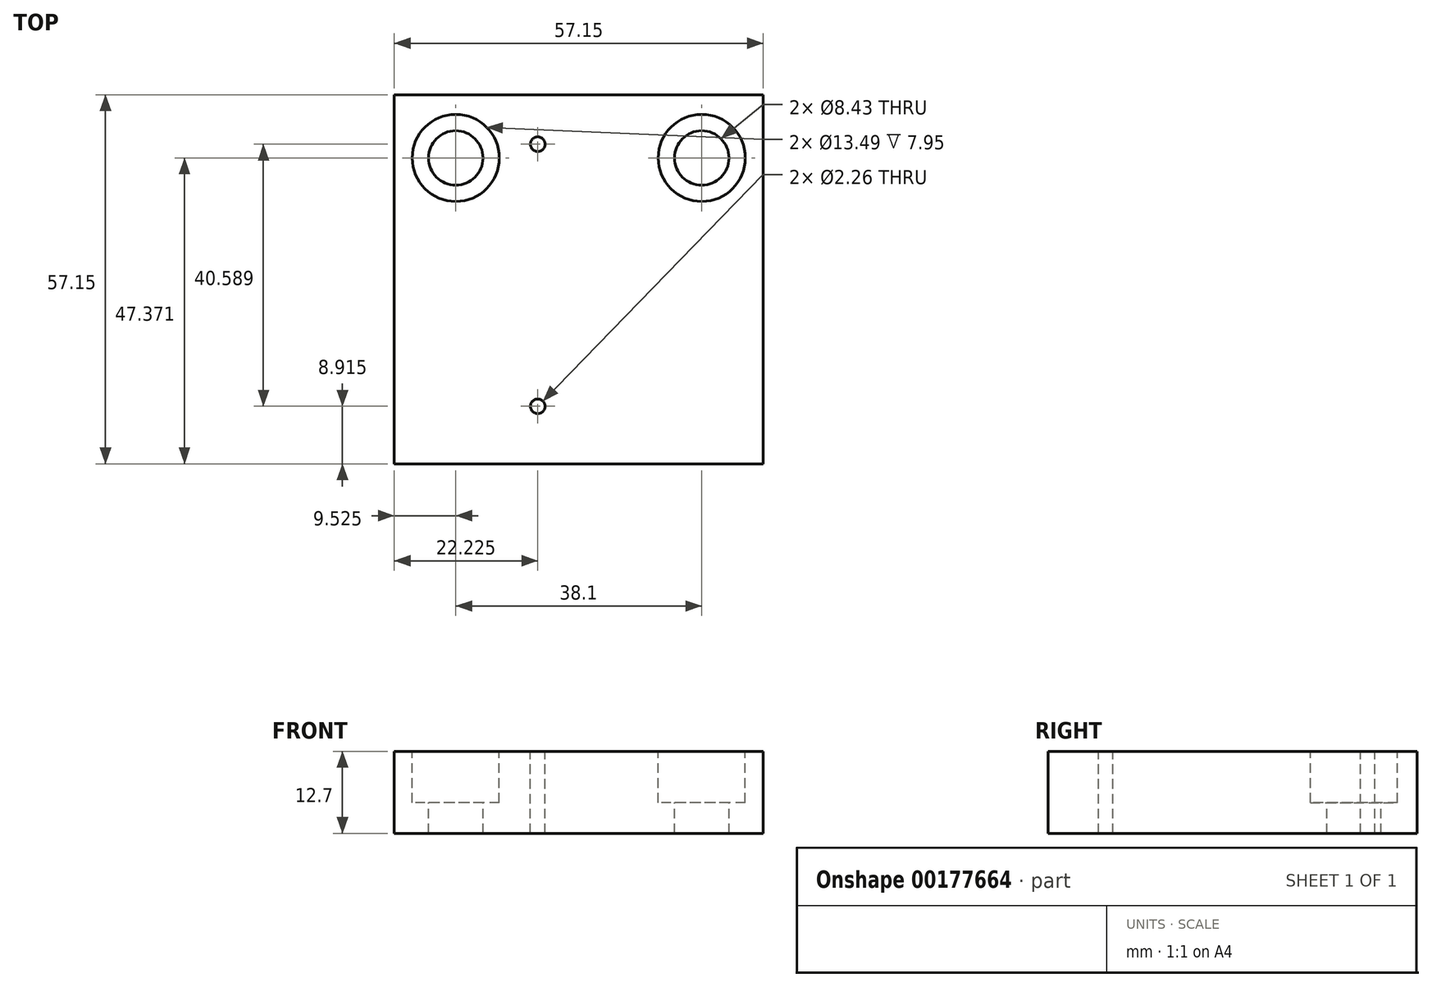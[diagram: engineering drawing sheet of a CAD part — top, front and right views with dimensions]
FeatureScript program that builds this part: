
annotation { "Feature Type Name" : "Feature", "Feature Type Description" : "" }
export const myFeature = defineFeature(function(context is Context, id is Id, definition is map)
    precondition{}
    {
        {
            var Q0;
            Q0=qCreatedBy(makeId("Top.planeOp"),FACE);
            var sketch = newSketch(context, id + "F0", { "sketchPlane" : qUnion([Q0])});
            skLineSegment(sketch, "E0.bottom", {"start": v(0, 0) * mm, "end": v(57.15, 0) * mm});
            skLineSegment(sketch, "E0.top", {"start": v(0, -57.15) * mm, "end": v(57.15, -57.15) * mm});
            skLineSegment(sketch, "E0.left", {"start": v(0, 0) * mm, "end": v(0, -57.15) * mm});
            skLineSegment(sketch, "E0.right", {"start": v(57.15, 0) * mm, "end": v(57.15, -57.15) * mm});
            skSolve(sketch);
        }
        {
            var Q0;
            Q0 = qSketchRegion(id + "F0", true);
            extrude(context, id + "F1", {"entities" : qUnion([Q0]), "depth" : 12.7 * mm});
        }
        {
            var Q0;
            Q0=makeQuery(id+"F1.opExtrude","CAP_FACE",FACE,{"disambiguationData":[OSD([sQuery(id+"F0.wireOp",EDGE,"E0.bottom"),sQuery(id+"F0.wireOp",EDGE,"E0.top"),sQuery(id+"F0.wireOp",EDGE,"E0.left"),sQuery(id+"F0.wireOp",EDGE,"E0.right")])],"isStart":false});
            var sketch = newSketch(context, id + "F2", { "sketchPlane" : qUnion([Q0])});
            skPoint(sketch, "E1", {"position": v(9.53, -9.78) * mm});
            skPoint(sketch, "E2", {"position": v(47.63, -9.78) * mm});
            skCircle(sketch, "E3", {"center": v(9.53, -9.78) * mm, "radius": 4.22 * mm});
            skCircle(sketch, "E4", {"center": v(47.63, -9.78) * mm, "radius": 4.22 * mm});
            skSolve(sketch);
        }
        {
            var Q0;
            Q0 = qSketchRegion(id + "F2", true);
            extrude(context, id + "F3", {"entities" : qUnion([Q0]), "operationType" : NewBodyOperationType.REMOVE, "endBound" : BoundingType.THROUGH_ALL, "oppositeDirection" : true, "depth" : 25.4 * mm});
        }
        {
            var Q0;
            Q0=makeQuery(id+"F1.opExtrude","CAP_FACE",FACE,{"disambiguationData":[OSD([sQuery(id+"F0.wireOp",EDGE,"E0.bottom"),sQuery(id+"F0.wireOp",EDGE,"E0.top"),sQuery(id+"F0.wireOp",EDGE,"E0.left"),sQuery(id+"F0.wireOp",EDGE,"E0.right")])],"isStart":false});
            var sketch = newSketch(context, id + "F4", { "sketchPlane" : qUnion([Q0])});
            skCircle(sketch, "E5", {"center": v(9.53, -9.78) * mm, "radius": 6.74 * mm});
            skCircle(sketch, "E6", {"center": v(47.63, -9.78) * mm, "radius": 6.74 * mm});
            skSolve(sketch);
        }
        {
            var Q0;
            Q0 = qSketchRegion(id + "F4", true);
            extrude(context, id + "F5", {"entities" : qUnion([Q0]), "operationType" : NewBodyOperationType.REMOVE, "oppositeDirection" : true, "depth" : 7.95 * mm});
        }
        {
            var Q0;
            Q0=makeQuery(id+"F1.opExtrude","CAP_FACE",FACE,{"disambiguationData":[OSD([sQuery(id+"F0.wireOp",EDGE,"E0.bottom"),sQuery(id+"F0.wireOp",EDGE,"E0.top"),sQuery(id+"F0.wireOp",EDGE,"E0.left"),sQuery(id+"F0.wireOp",EDGE,"E0.right")])],"isStart":false});
            var sketch = newSketch(context, id + "F6", { "sketchPlane" : qUnion([Q0])});
            skPoint(sketch, "E7", {"position": v(22.23, -7.65) * mm});
            skPoint(sketch, "E8", {"position": v(22.23, -48.23) * mm});
            skSolve(sketch);
        }
        {
            var Q0;
            Q0=sQuery(id+"F6.wireOp",VERTEX,"E7");
            var Q1;
            Q1=sQuery(id+"F6.wireOp",VERTEX,"E8");
            var Q2;
            Q2=makeQuery(id+"F1.opExtrude","SWEPT_BODY",BODY,{"disambiguationData":[OSD([sQuery(id+"F0.wireOp",EDGE,"E0.bottom"),sQuery(id+"F0.wireOp",EDGE,"E0.top"),sQuery(id+"F0.wireOp",EDGE,"E0.left"),sQuery(id+"F0.wireOp",EDGE,"E0.right")])]});
            hole(context, id + "F7", {"style" : HoleStyle.SIMPLE, "endStyle" : HoleEndStyle.THROUGH, "standardTappedOrClearance" : lookupTablePath({ "standard" : "ANSI", "engagement" : "75%", "pitch" : "40 tpi", "size" : "#4", "type" : "Tapped" }), "standardBlindInLast" : lookupTablePath({ "standard" : "ANSI", "engagement" : "75%", "pitch" : "40 tpi", "size" : "#4", "type" : "Tapped" }), "holeDiameter" : 2.26 * mm, "startFromSketch" : true, "locations" : qUnion([Q0, Q1]), "scope" : qUnion([Q2]), "isTappedThrough" : true, "majorDiameter" : 2.84 * mm, "showTappedDepth" : true});
        }
    });
